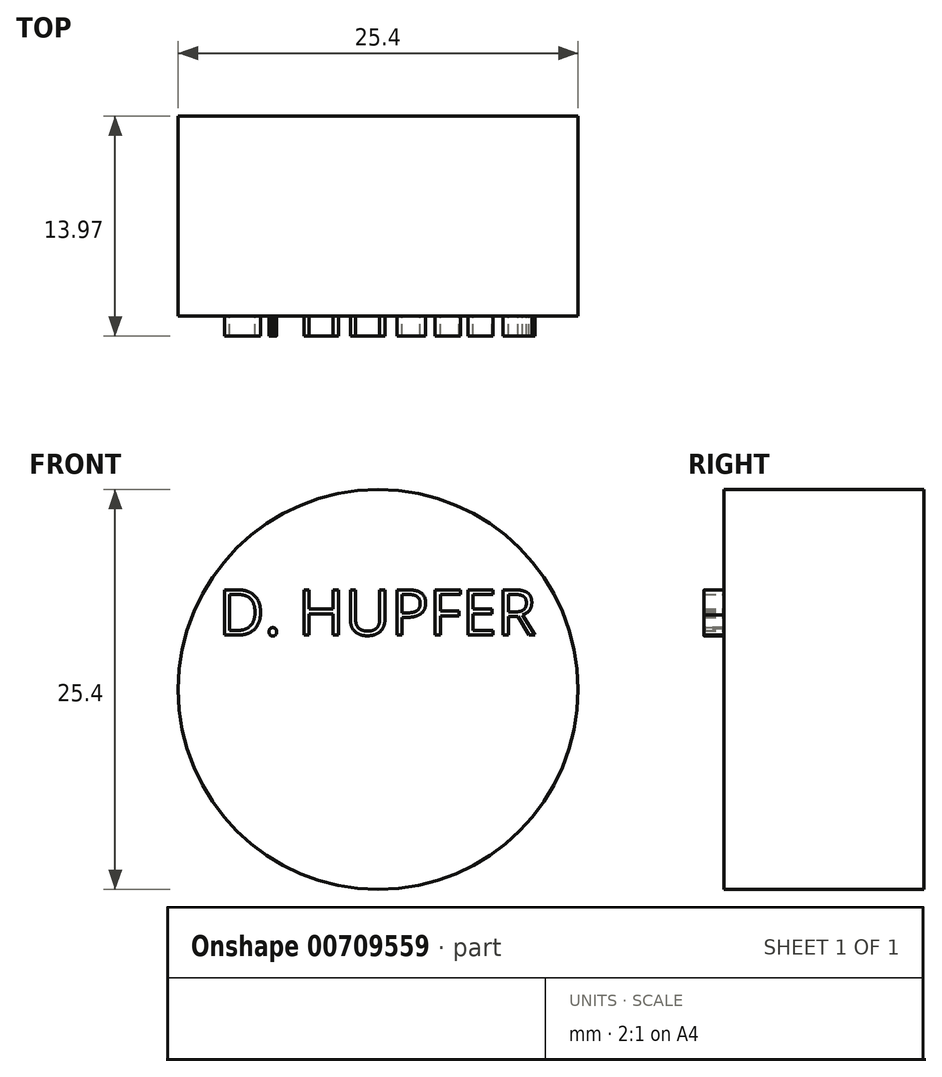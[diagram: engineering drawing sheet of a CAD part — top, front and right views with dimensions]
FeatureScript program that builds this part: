
annotation { "Feature Type Name" : "Feature", "Feature Type Description" : "" }
export const myFeature = defineFeature(function(context is Context, id is Id, definition is map)
    precondition{}
    {
        {
            var Q0;
            Q0=qCreatedBy(makeId("Front.planeOp"),FACE);
            var sketch = newSketch(context, id + "F0", { "sketchPlane" : qUnion([Q0])});
            skCircle(sketch, "E0", {"center": v(34.74, 37.15) * mm, "radius": 12.7 * mm});
            skSolve(sketch);
        }
        {
            var Q0;
            Q0 = qSketchRegion(id + "F0", true);
            extrude(context, id + "F1", {"entities" : qUnion([Q0]), "depth" : 12.7 * mm, "offsetDistance" : 25.4 * mm});
        }
        {
            var Q0;
            Q0=makeQuery(id+"F1.opExtrude","CAP_FACE",FACE,{"disambiguationData":[OSD([sQuery(id+"F0.wireOp",EDGE,"E0")])],"isStart":false});
            var sketch = newSketch(context, id + "F2", { "sketchPlane" : qUnion([Q0])});
            skText(sketch, "E1", { "text": "D. HUPFER", "fontName": "OpenSans-Regular.ttf"});
            const initialGuessF2  = {"E1": [0.02458, 0.0406, 1, 0, 0.0029]};
            skSetInitialGuess(sketch, initialGuessF2);
            skSolve(sketch);
        }
        {
            var Q0;
            Q0 = qSketchRegion(id + "F2", true);
            extrude(context, id + "F3", {"entities" : qUnion([Q0]), "operationType" : NewBodyOperationType.ADD, "depth" : 1.27 * mm, "offsetDistance" : 25.4 * mm});
        }
    });
